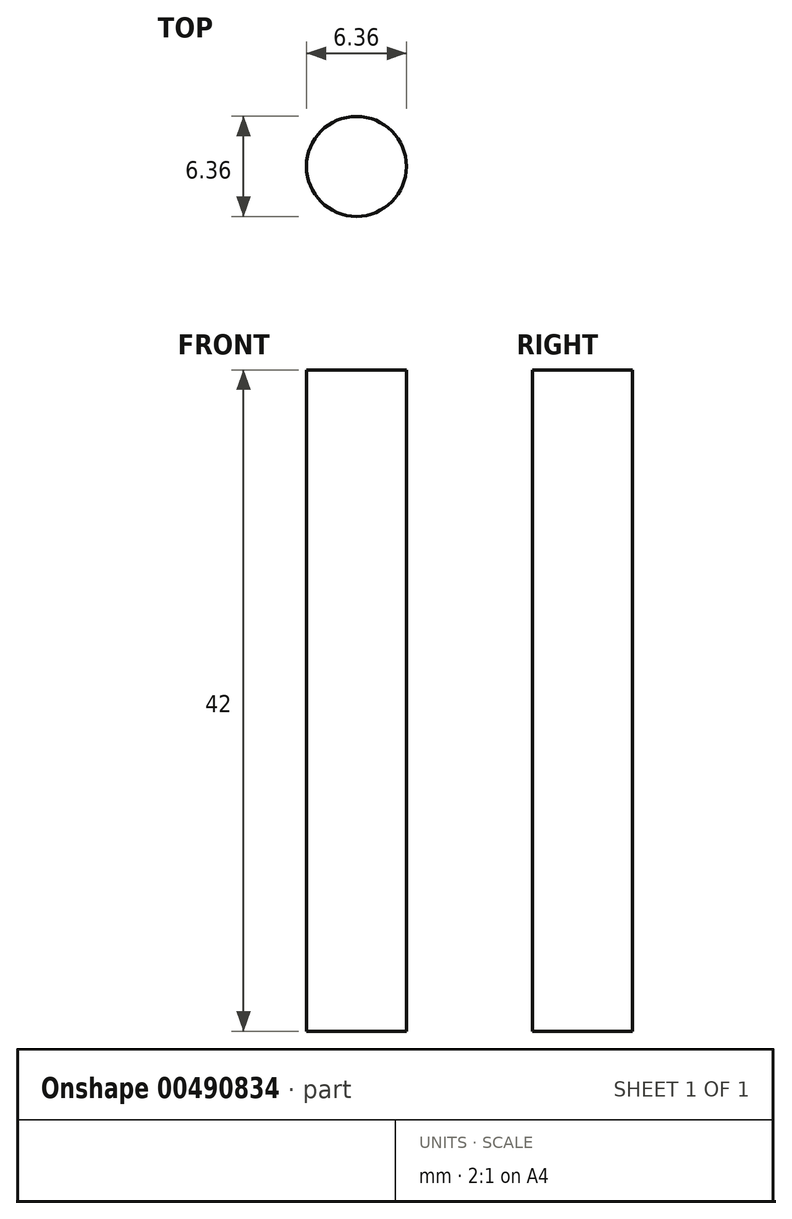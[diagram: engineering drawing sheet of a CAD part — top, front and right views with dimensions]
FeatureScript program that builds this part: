
annotation { "Feature Type Name" : "Feature", "Feature Type Description" : "" }
export const myFeature = defineFeature(function(context is Context, id is Id, definition is map)
    precondition{}
    {
        {
            var Q0;
            Q0=qCreatedBy(makeId("Top.planeOp"),FACE);
            var sketch = newSketch(context, id + "F0", { "sketchPlane" : qUnion([Q0])});
            skCircle(sketch, "E0", {"center": v(0, 0) * mm, "radius": 3.18 * mm});
            skSolve(sketch);
        }
        {
            var Q0;
            Q0 = qSketchRegion(id + "F0", true);
            extrude(context, id + "F1", {"entities" : qUnion([Q0]), "depth" : 42 * mm, "offsetDistance" : 25 * mm});
        }
    });
